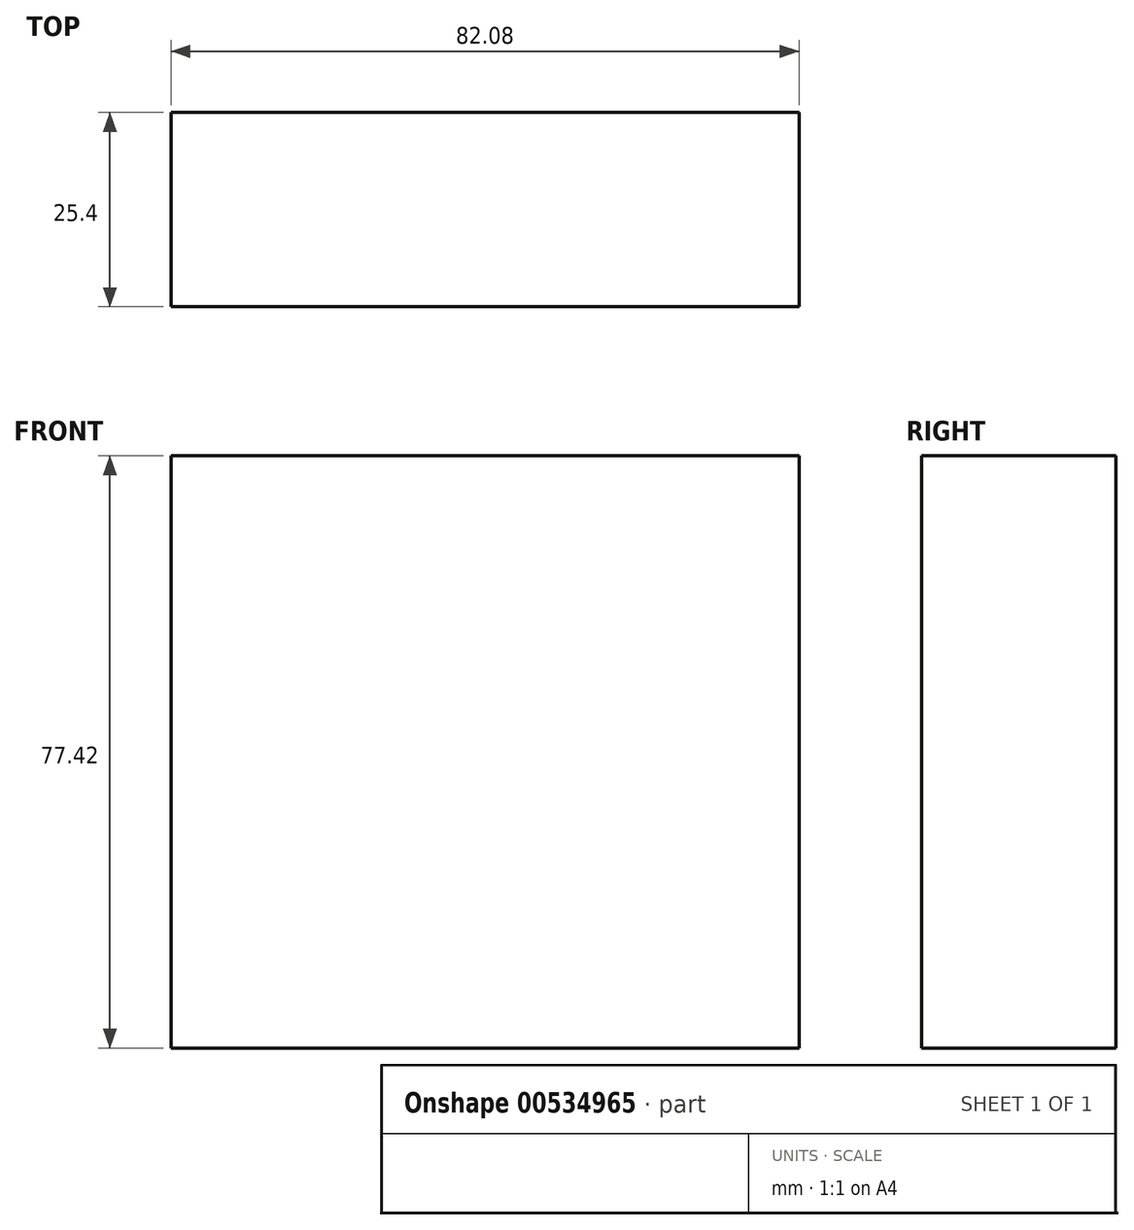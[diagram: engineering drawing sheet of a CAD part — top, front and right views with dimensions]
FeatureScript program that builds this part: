
annotation { "Feature Type Name" : "Feature", "Feature Type Description" : "" }
export const myFeature = defineFeature(function(context is Context, id is Id, definition is map)
    precondition{}
    {
        {
            var Q0;
            Q0=qCreatedBy(makeId("Front.planeOp"),FACE);
            var sketch = newSketch(context, id + "F0", { "sketchPlane" : qUnion([Q0])});
            skLineSegment(sketch, "E0.bottom", {"start": v(-41.04, 38.71) * mm, "end": v(41.04, 38.71) * mm});
            skLineSegment(sketch, "E0.top", {"start": v(-41.04, -38.71) * mm, "end": v(41.04, -38.71) * mm});
            skLineSegment(sketch, "E0.left", {"start": v(-41.04, 38.71) * mm, "end": v(-41.04, -38.71) * mm});
            skLineSegment(sketch, "E0.right", {"start": v(41.04, 38.71) * mm, "end": v(41.04, -38.71) * mm});
            skPoint(sketch, "E0.middle", {"position": v(0, 0) * mm});
            skSolve(sketch);
        }
        {
            var Q0;
            Q0=makeQuery(id+"F0.imprint","IMPRINT",FACE,{"disambiguationData":[TD([[makeQuery(id+"F0.imprint","IMPRINT",EDGE,{"derivedFrom":sQuery(id+"F0.wireOp",EDGE,"E0.bottom")}),-1.0]])]});
            extrude(context, id + "F1", {"entities" : qUnion([Q0]), "depth" : 25.4 * mm, "offsetDistance" : 25.4 * mm});
        }
    });
